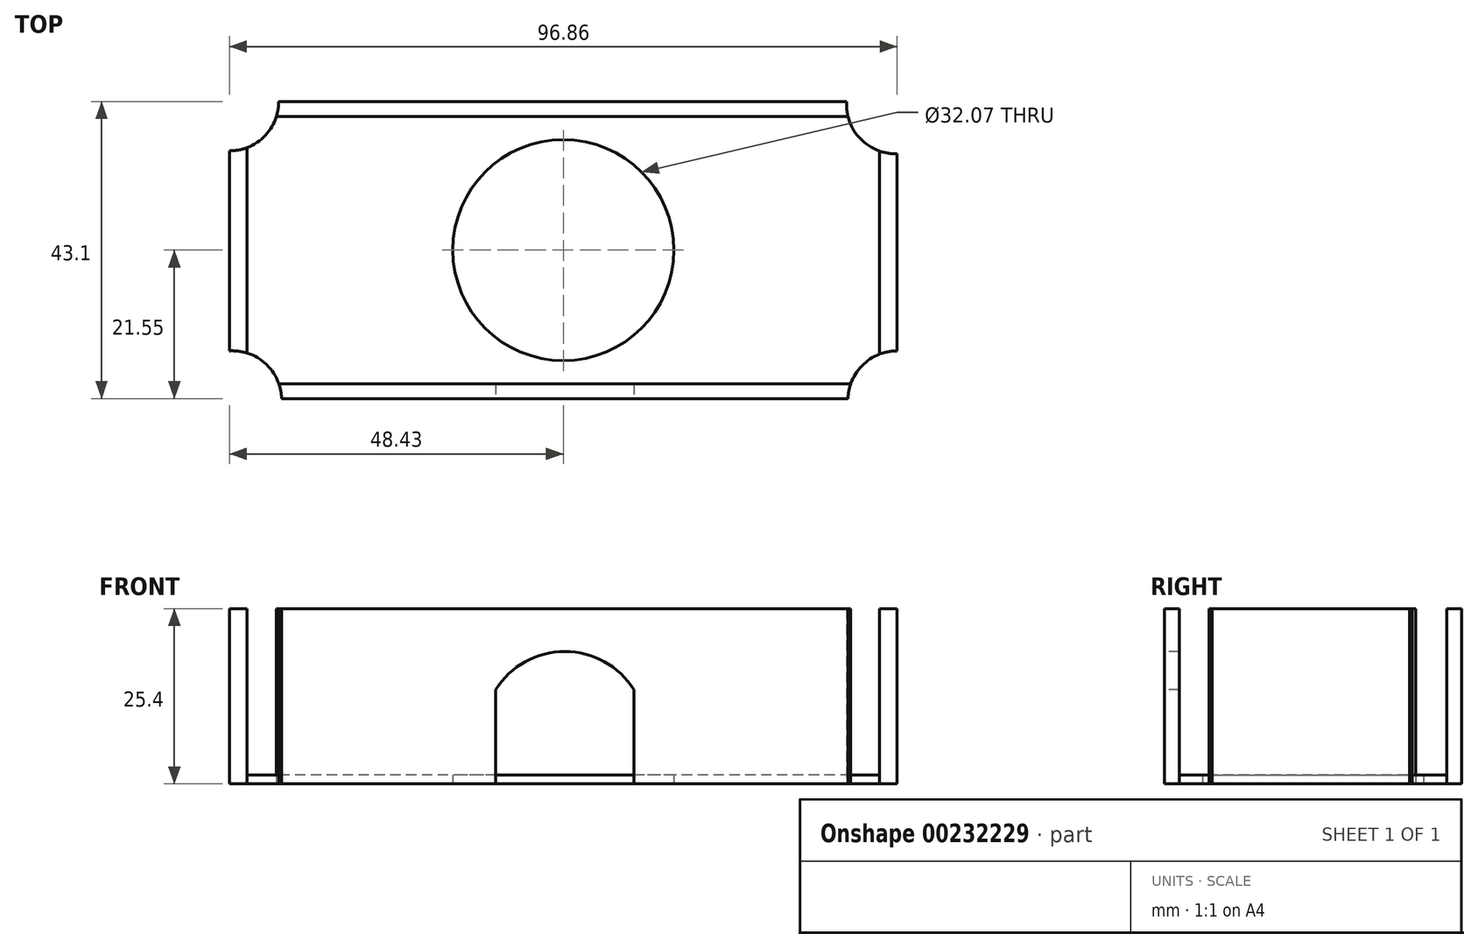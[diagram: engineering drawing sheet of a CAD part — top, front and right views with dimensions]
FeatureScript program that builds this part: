
annotation { "Feature Type Name" : "Feature", "Feature Type Description" : "" }
export const myFeature = defineFeature(function(context is Context, id is Id, definition is map)
    precondition{}
    {
        {
            var Q0;
            Q0=qCreatedBy(makeId("Top.planeOp"),FACE);
            var sketch = newSketch(context, id + "F0", { "sketchPlane" : qUnion([Q0])});
            skLineSegment(sketch, "E0.bottom", {"start": v(41.1, 21.55) * mm, "end": v(-41.3, 21.55) * mm});
            skLineSegment(sketch, "E0.top", {"start": v(41.3, -21.55) * mm, "end": v(-40.87, -21.55) * mm});
            skLineSegment(sketch, "E0.left", {"start": v(48.43, 13.98) * mm, "end": v(48.43, -14.63) * mm});
            skLineSegment(sketch, "E0.right", {"start": v(-48.43, 14.4) * mm, "end": v(-48.43, -14.63) * mm});
            skPoint(sketch, "E0.middle", {"position": v(0, 0) * mm});
            skCircle(sketch, "E1", {"center": v(-48.43, 21.55) * mm, "radius": 7.14 * mm});
            skCircle(sketch, "E2", {"center": v(48.22, 21.12) * mm, "radius": 7.14 * mm});
            skCircle(sketch, "E3", {"center": v(48.43, -21.77) * mm, "radius": 7.14 * mm});
            skCircle(sketch, "E4", {"center": v(-48.01, -21.75) * mm, "radius": 7.14 * mm});
            skPoint(sketch, "E5.orphan", {"position": v(48.43, 21.55) * mm});
            skPoint(sketch, "E6.orphan", {"position": v(48.43, -21.55) * mm});
            skPoint(sketch, "E7.orphan", {"position": v(-48.43, -21.55) * mm});
            skLineSegment(sketch, "E8.bottom", {"start": v(41.7, -19.42) * mm, "end": v(-41.27, -19.42) * mm});
            skLineSegment(sketch, "E8.top", {"start": v(41.29, 19.42) * mm, "end": v(-41.62, 19.42) * mm});
            skLineSegment(sketch, "E8.left", {"start": v(45.87, -15.1) * mm, "end": v(45.87, 14.38) * mm});
            skLineSegment(sketch, "E8.right", {"start": v(-45.87, -14.94) * mm, "end": v(-45.87, 14.88) * mm});
            skPoint(sketch, "E9.orphan", {"position": v(45.87, 19.42) * mm});
            skPoint(sketch, "E10.orphan", {"position": v(45.87, -19.42) * mm});
            skPoint(sketch, "E11.orphan", {"position": v(-45.87, -19.42) * mm});
            skPoint(sketch, "E12.orphan", {"position": v(-45.87, 19.42) * mm});
            skCircle(sketch, "E13", {"center": v(0, 0) * mm, "radius": 16.03 * mm});
            skSolve(sketch);
        }
        {
            var Q0;
            {var subQ0=sQuery(id+"F0.wireOp",EDGE,"E0.bottom");Q0=makeQuery(id+"F0.imprint","IMPRINT",FACE,{"disambiguationData":[TD([[makeQuery(id+"F0.imprint","IMPRINT",EDGE,{"derivedFrom":subQ0}),1.0]])]});}
            var Q1;
            {var subQ0=sQuery(id+"F0.wireOp",EDGE,"E0.right");Q1=makeQuery(id+"F0.imprint","IMPRINT",FACE,{"disambiguationData":[TD([[makeQuery(id+"F0.imprint","IMPRINT",EDGE,{"derivedFrom":subQ0}),1.0]])]});}
            var Q2;
            {var subQ0=sQuery(id+"F0.wireOp",EDGE,"E0.top");Q2=makeQuery(id+"F0.imprint","IMPRINT",FACE,{"disambiguationData":[TD([[makeQuery(id+"F0.imprint","IMPRINT",EDGE,{"derivedFrom":subQ0}),-1.0]])]});}
            var Q3;
            {var subQ0=sQuery(id+"F0.wireOp",EDGE,"E0.left");Q3=makeQuery(id+"F0.imprint","IMPRINT",FACE,{"disambiguationData":[TD([[makeQuery(id+"F0.imprint","IMPRINT",EDGE,{"derivedFrom":subQ0}),-1.0]])]});}
            extrude(context, id + "F1", {"entities" : qUnion([Q0, Q1, Q2, Q3]), "depth" : 25.4 * mm});
        }
        {
            var Q0;
            Q0=sQuery(id+"F0.wireOp",EDGE,"E1");
            var Q1;
            Q1=sQuery(id+"F0.wireOp",EDGE,"E2");
            var Q2;
            Q2=sQuery(id+"F0.wireOp",EDGE,"E3");
            var Q3;
            Q3=sQuery(id+"F0.wireOp",EDGE,"E4");
            extrude(context, id + "F2", {"bodyType" : ToolBodyType.SURFACE, "surfaceEntities" : qUnion([Q0, Q1, Q2, Q3]), "depth" : 31.75 * mm});
        }
        {
            var Q0;
            Q0=makeQuery(id+"F1.opExtrude","SWEPT_FACE",FACE,{"disambiguationData":[OSD([sQuery(id+"F0.wireOp",EDGE,"E0.top")])]});
            var sketch = newSketch(context, id + "F3", { "sketchPlane" : qUnion([Q0])});
            skLineSegment(sketch, "E14.bottom", {"start": v(-9.81, 0) * mm, "end": v(10.24, 0) * mm});
            skLineSegment(sketch, "E14.left", {"start": v(-9.81, 0) * mm, "end": v(-9.81, 13.66) * mm});
            skLineSegment(sketch, "E14.right", {"start": v(10.24, 0) * mm, "end": v(10.24, 13.66) * mm});
            skArc(sketch, "E15", {"start": v(10.24, 13.66) * mm, "mid": v(0.21, 19.21) * mm, "end": v(-9.81, 13.66) * mm});
            skSolve(sketch);
        }
        {
            var Q0;
            Q0=makeQuery(id+"F3.imprint","IMPRINT",FACE,{"disambiguationData":[TD([[makeQuery(id+"F3.imprint","IMPRINT",EDGE,{"derivedFrom":sQuery(id+"F3.wireOp",EDGE,"E14.bottom")}),-1.0]])]});
            extrude(context, id + "F4", {"entities" : qUnion([Q0]), "operationType" : NewBodyOperationType.REMOVE, "oppositeDirection" : true, "depth" : 2.3 * mm});
        }
        {
            var Q0;
            Q0=sQuery(id+"F0.wireOp",EDGE,"E13");
            extrude(context, id + "F5", {"bodyType" : ToolBodyType.SURFACE, "surfaceEntities" : qUnion([Q0]), "depth" : 50.8 * mm});
        }
        {
            var Q0;
            {var subQ0=sQuery(id+"F0.wireOp",EDGE,"E8.bottom");Q0=makeQuery(id+"F0.imprint","IMPRINT",FACE,{"disambiguationData":[TD([[makeQuery(id+"F0.imprint","IMPRINT",EDGE,{"derivedFrom":subQ0}),-1.0]])]});}
            extrude(context, id + "F6", {"entities" : qUnion([Q0]), "depth" : 1.27 * mm});
        }
    });
